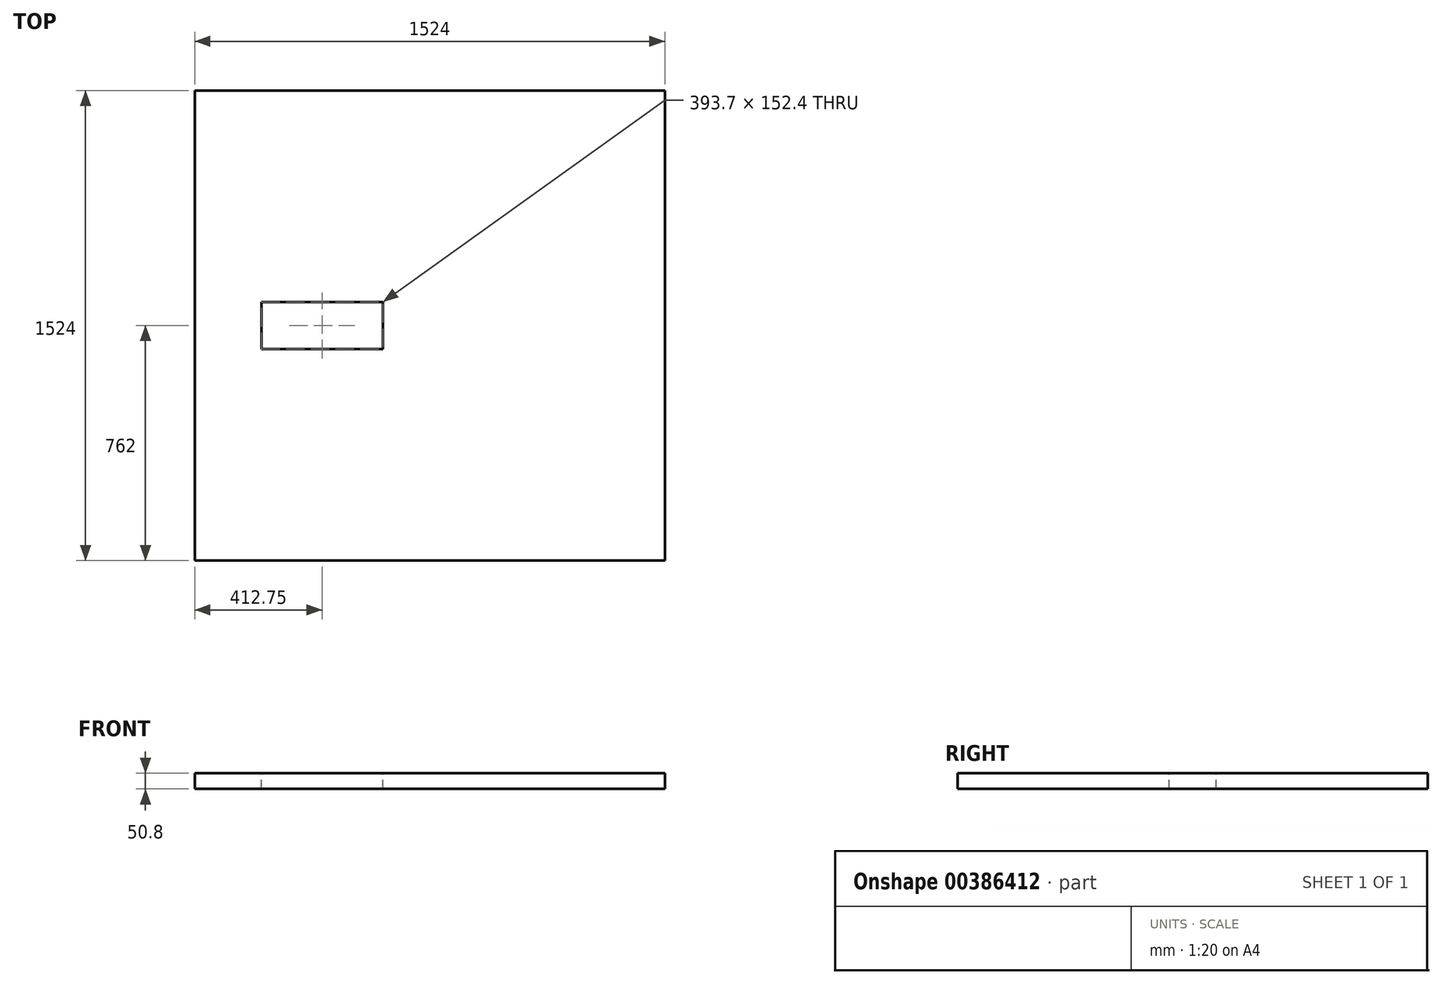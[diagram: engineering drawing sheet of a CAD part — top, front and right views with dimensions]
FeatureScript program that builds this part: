
annotation { "Feature Type Name" : "Feature", "Feature Type Description" : "" }
export const myFeature = defineFeature(function(context is Context, id is Id, definition is map)
    precondition{}
    {
        {
            var Q0;
            Q0=qCreatedBy(makeId("Top.planeOp"),FACE);
            var sketch = newSketch(context, id + "F0", { "sketchPlane" : qUnion([Q0])});
            skLineSegment(sketch, "E0.bottom", {"start": v(-762, 762) * mm, "end": v(762, 762) * mm});
            skLineSegment(sketch, "E0.top", {"start": v(-762, -762) * mm, "end": v(762, -762) * mm});
            skLineSegment(sketch, "E0.left", {"start": v(-762, 762) * mm, "end": v(-762, -762) * mm});
            skLineSegment(sketch, "E0.right", {"start": v(762, 762) * mm, "end": v(762, -762) * mm});
            skPoint(sketch, "E0.middle", {"position": v(0, 0) * mm});
            skSolve(sketch);
        }
        {
            var Q0;
            Q0 = qSketchRegion(id + "F0", true);
            extrude(context, id + "F1", {"entities" : qUnion([Q0]), "depth" : 50.8 * mm});
        }
        {
            var Q0;
            Q0=makeQuery(id+"F1.opExtrude","CAP_FACE",FACE,{"disambiguationData":[OSD([sQuery(id+"F0.wireOp",EDGE,"E0.bottom"),sQuery(id+"F0.wireOp",EDGE,"E0.top"),sQuery(id+"F0.wireOp",EDGE,"E0.left"),sQuery(id+"F0.wireOp",EDGE,"E0.right")])],"isStart":false});
            var sketch = newSketch(context, id + "F2", { "sketchPlane" : qUnion([Q0])});
            skLineSegment(sketch, "E1.bottom", {"start": v(-571.5, 571.5) * mm, "end": v(571.5, 571.5) * mm});
            skLineSegment(sketch, "E1.top", {"start": v(-571.5, -571.5) * mm, "end": v(571.5, -571.5) * mm});
            skLineSegment(sketch, "E1.left", {"start": v(-571.5, 571.5) * mm, "end": v(-571.5, -571.5) * mm});
            skLineSegment(sketch, "E1.right", {"start": v(571.5, 571.5) * mm, "end": v(571.5, -571.5) * mm});
            skPoint(sketch, "E1.middle", {"position": v(0, 0) * mm});
            skLineSegment(sketch, "E2.0", {"start": v(-546.1, 546.1) * mm, "end": v(546.1, 546.1) * mm});
            skLineSegment(sketch, "E2.1", {"start": v(-546.1, 546.1) * mm, "end": v(-546.1, -546.1) * mm});
            skLineSegment(sketch, "E2.2", {"start": v(-546.1, -546.1) * mm, "end": v(546.1, -546.1) * mm});
            skLineSegment(sketch, "E2.3", {"start": v(546.1, 546.1) * mm, "end": v(546.1, -546.1) * mm});
            skLineSegment(sketch, "E3", {"start": v(-571.5, 0) * mm, "end": v(-152.4, 0) * mm});
            skLineSegment(sketch, "E4.0", {"start": v(-571.5, -76.2) * mm, "end": v(-152.4, -76.2) * mm});
            skLineSegment(sketch, "E5.0", {"start": v(-571.5, 76.2) * mm, "end": v(-152.4, 76.2) * mm});
            skLineSegment(sketch, "E6", {"start": v(-152.4, 76.2) * mm, "end": v(-152.4, -76.2) * mm});
            skSolve(sketch);
        }
        {
            var Q0;
            {var subQ0=sQuery(id+"F2.wireOp",EDGE,"E3");var subQ1=sQuery(id+"F2.wireOp",EDGE,"E2.1");var subQ2=makeQuery(id+"F2.imprint","INTERSECT",VERTEX,{"derivedFrom":[subQ1,subQ0]});Q0=makeQuery(id+"F2.imprint","IMPRINT",FACE,{"disambiguationData":[TD([[makeQuery(id+"F2.imprint","IMPRINT",EDGE,{"disambiguationData":[TD([[subQ2,-1.0]])],"derivedFrom":subQ1}),1.0]])]});}
            var Q1;
            {var subQ0=sQuery(id+"F2.wireOp",EDGE,"E5.0");var subQ1=sQuery(id+"F2.wireOp",EDGE,"E2.1");var subQ2=makeQuery(id+"F2.imprint","INTERSECT",VERTEX,{"derivedFrom":[subQ1,subQ0]});Q1=makeQuery(id+"F2.imprint","IMPRINT",FACE,{"disambiguationData":[TD([[makeQuery(id+"F2.imprint","IMPRINT",EDGE,{"disambiguationData":[TD([[subQ2,-1.0]])],"derivedFrom":subQ1}),1.0]])]});}
            extrude(context, id + "F3", {"entities" : qUnion([Q0, Q1]), "operationType" : NewBodyOperationType.REMOVE, "oppositeDirection" : true, "depth" : 314.96 * mm});
        }
        {
            var Q0;
            Q0=makeQuery(id+"F1.opExtrude","CAP_FACE",FACE,{"disambiguationData":[OSD([sQuery(id+"F0.wireOp",EDGE,"E0.bottom"),sQuery(id+"F0.wireOp",EDGE,"E0.top"),sQuery(id+"F0.wireOp",EDGE,"E0.left"),sQuery(id+"F0.wireOp",EDGE,"E0.right")])],"isStart":true});
            var sketch = newSketch(context, id + "F4", { "sketchPlane" : qUnion([Q0])});
            skLineSegment(sketch, "E7.0", {"start": v(-571.5, 571.5) * mm, "end": v(571.5, 571.5) * mm});
            skLineSegment(sketch, "E7.1", {"start": v(571.5, -571.5) * mm, "end": v(571.5, 571.5) * mm});
            skLineSegment(sketch, "E7.2", {"start": v(-571.5, -571.5) * mm, "end": v(571.5, -571.5) * mm});
            skLineSegment(sketch, "E7.3", {"start": v(-571.5, -571.5) * mm, "end": v(-571.5, 571.5) * mm});
            skSolve(sketch);
        }
    });
